# Revit family: PRD_FrankeWS_WlMntdBbTps_WallOutlet_AQRM905_AQRM906_AQRM907
name_source: partatom
category: Plumbing Fixtures
revit_build: Autodesk Revit 2018 (Build: 20190510_1515(x64)
units: mm (PartAtom-declared; Revit-internal decimal feet)

## family parameters
Always vertical = Yes
Cut with Voids When Loaded = No
OmniClass Number = 23.45.55.14
OmniClass Title = Single Faucets
Part Type = Normal
Room Calculation Point = No
Round Connector Dimension = Use Diameter
Shared = No
Work Plane-Based = Yes

## types (3) — shared parameters
AssetType = Fixed
Category = Pr_40_20_87_93, Wall-mounted bib taps
Color = Chrome
Default Elevation = 750 mm  [stored 2.46063 ft]
DiameterNominal = 15 mm
DurationUnit = year
FaucetFunction = Mixed
FaucetMaterial = PRD_AR_ChromatedBrass_HighPolished
FaucetOperation = QuickAction
FaucetType = Bib
Features = polished chromium-plated brass
Finish = polished
FlowColdWater = 0.1 L/s
IfcExportAs = IfcValveType
IfcExportType = FAUCET
InletSize = DN 15
Manufacturer = KWC Group AG
ManufacturerName = KWC Group AG
ManufacturerURL = www.kwc.com
Material = Brass
ProductInformation = https://pim.kwc.com
TypeOfSpout = Wall outlet
URL = www.kwc.com
Uniclass2015Code = Pr_40_20_87_93
Uniclass2015Title = Wall-mounted bib taps
Uniclass2015Version = Products v1.17
Version = 1
VolumeFlowRate = 0.10 L/s at 3 bar
WarrantyDurationUnit = year
zero-valued in all types: NominalDepth, NominalHeight, NominalWidth

## per-type parameters (varying)
| type | BIMObjectName | Description | GrossWeight | ModelNumber | Name | NetWeight | SpoutProjection | Tap lentgh |
| AQRM905 | PRD_AR_WallMountedBibTaps_WallOutlet_AQRM905 | Wall outlet, DN 15, with theft-proof aerator, polished chromium-plated brass, projection 234 mm. | 1.36 kg | 2000100805 | Wall Outlet AQRM905 | 1.25 kg | 234.00 mm | 200 mm  [stored 0.656168 ft] |
| AQRM906 | PRD_AR_WallMountedBibTaps_WallOutlet_AQRM906 | Wall outlet, DN 15, with theft-proof aerator, polished chromium-plated brass, projection 165 mm. | 1.04 kg | 2000100806 | Wall Outlet AQRM906 | 0.92 kg | 165.00 mm | 131 mm  [stored 0.42979 ft] |
| AQRM907 | PRD_AR_WallMountedBibTaps_WallOutlet_AQRM907 | Wall outlet, DN 15, with theft-proof aerator, polished chromium-plated brass, projection 78 mm. | 0.62 kg | 2000100809 | Wall Outlet AQRM907 | 0.56 kg | 78.00 mm | 44 mm  [stored 0.144357 ft] |

note: column(s) folded — value = type name in every type: Model, ModelReference

note: [stored X ft] marks values corroborated as IEEE doubles in the binary element streams (Revit-internal decimal feet)

## geometry (parser evidence)
native form markers: Sweep x2
no freeform markers — native parametric forms only
